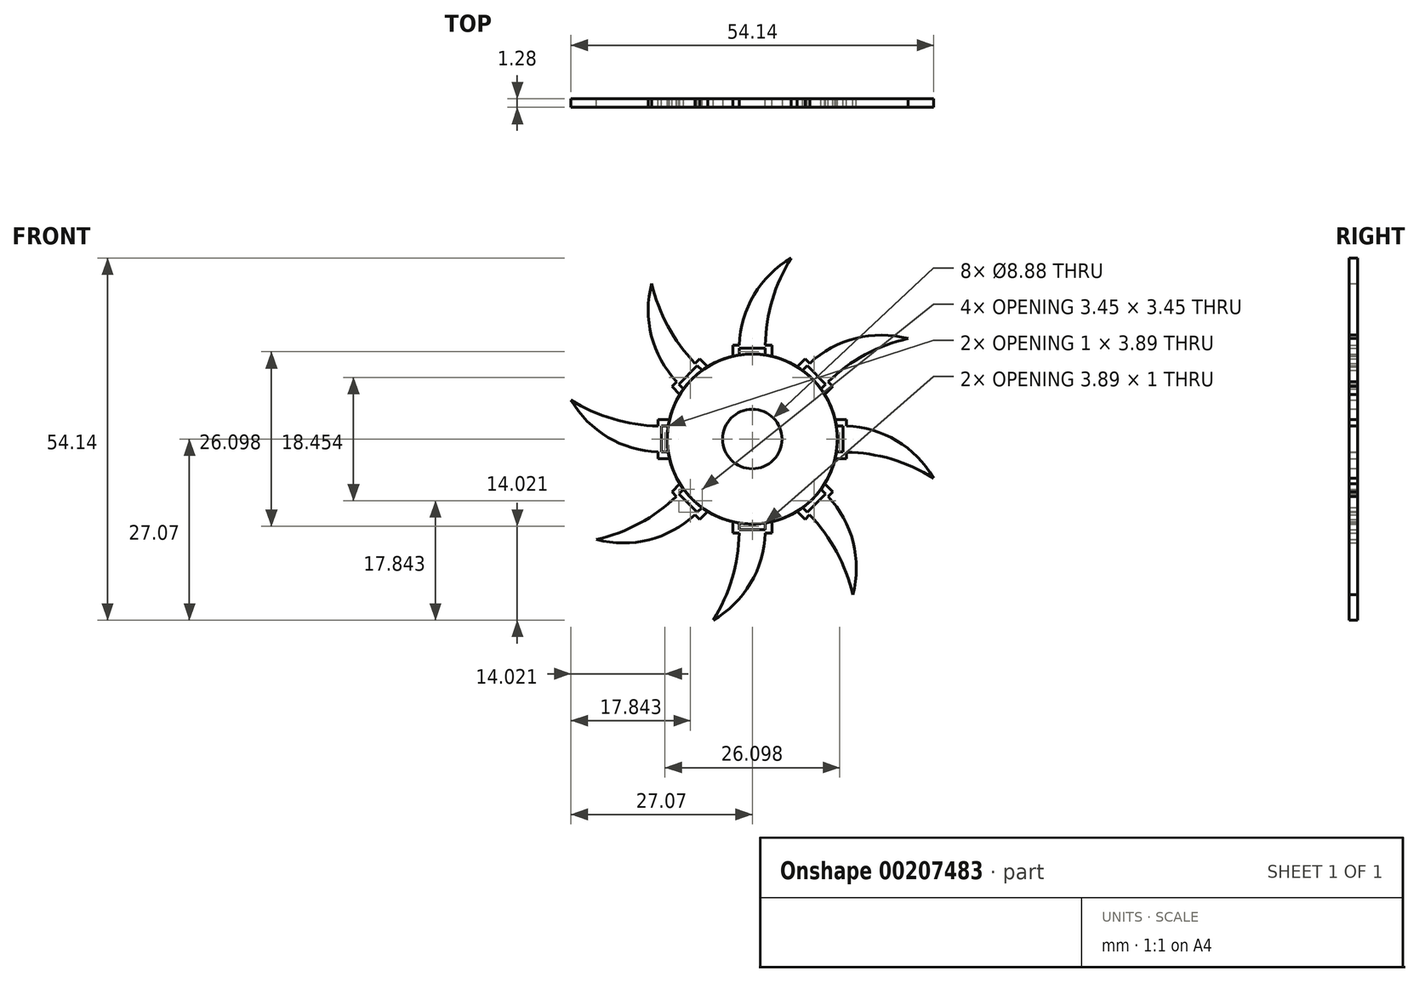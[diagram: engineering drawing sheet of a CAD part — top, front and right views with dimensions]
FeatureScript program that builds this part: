
annotation { "Feature Type Name" : "Feature", "Feature Type Description" : "" }
export const myFeature = defineFeature(function(context is Context, id is Id, definition is map)
    precondition{}
    {
        {
            var Q0;
            Q0=qCreatedBy(makeId("Front.planeOp"),FACE);
            var sketch = newSketch(context, id + "F0", { "sketchPlane" : qUnion([Q0])});
            skCircle(sketch, "E0", {"center": v(0, 0) * mm, "radius": 12.7 * mm});
            skSolve(sketch);
        }
        {
            var Q0;
            Q0=qSketchRegion(id+"F0",true);
            extrude(context, id + "F1", {"entities" : qUnion([Q0]), "endBound" : BoundingType.SYMMETRIC, "depth" : 1.27 * mm});
        }
        {
            var Q0;
            Q0=qCreatedBy(makeId("Front.planeOp"),FACE);
            var sketch = newSketch(context, id + "F2", { "sketchPlane" : qUnion([Q0])});
            skPoint(sketch, "E1.middle", {"position": v(0, 12.38) * mm});
            skLineSegment(sketch, "E2.bottom", {"start": v(1.94, 13.55) * mm, "end": v(-1.94, 13.55) * mm});
            skLineSegment(sketch, "E2.top", {"start": v(1.94, 11.21) * mm, "end": v(-1.94, 11.21) * mm});
            skLineSegment(sketch, "E2.left", {"start": v(1.94, 13.55) * mm, "end": v(1.94, 11.21) * mm});
            skLineSegment(sketch, "E2.right", {"start": v(-1.94, 13.55) * mm, "end": v(-1.94, 11.21) * mm});
            skArc(sketch, "E3", {"start": v(5.83, 27.07) * mm, "mid": v(0.14, 21.34) * mm, "end": v(-1.94, 13.55) * mm});
            skArc(sketch, "E4", {"start": v(5.83, 27.07) * mm, "mid": v(2.93, 20.58) * mm, "end": v(1.94, 13.55) * mm});
            skLineSegment(sketch, "E5.bottom", {"start": v(2.93, 10.7) * mm, "end": v(-2.93, 10.7) * mm});
            skLineSegment(sketch, "E5.top", {"start": v(2.93, 14.05) * mm, "end": v(-2.93, 14.05) * mm});
            skLineSegment(sketch, "E5.left", {"start": v(2.93, 10.7) * mm, "end": v(2.93, 14.05) * mm});
            skLineSegment(sketch, "E5.right", {"start": v(-2.93, 10.7) * mm, "end": v(-2.93, 14.05) * mm});
            skSolve(sketch);
        }
        {
            var Q0;
            Q0=qSketchRegion(id+"F2",true);
            extrude(context, id + "F3", {"entities" : qUnion([Q0]), "operationType" : NewBodyOperationType.ADD, "endBound" : BoundingType.SYMMETRIC, "depth" : 1.27 * mm});
        }
        {
            var Q0;
            Q0=makeQuery(id+"F1.opExtrude","SWEPT_BODY",BODY,{"disambiguationData":[OSD([sQuery(id+"F0.wireOp",EDGE,"E0")])]});
            var Q1;
            Q1=sQuery(id+"F0.wireOp",EDGE,"E0");
            circularPattern(context, id + "F4", {"entities" : qUnion([Q0]), "axis" : qUnion([Q1]), "angle" : 360 * degree, "instanceCount" : 8, "equalSpace" : true});
        }
        {
            var Q0;
            Q0=qCreatedBy(makeId("Front.planeOp"),FACE);
            var sketch = newSketch(context, id + "F5", { "sketchPlane" : qUnion([Q0])});
            skCircle(sketch, "E6", {"center": v(0, 0) * mm, "radius": 4.44 * mm});
            skSolve(sketch);
        }
        {
            var Q0;
            Q0=qSketchRegion(id+"F5",true);
            extrude(context, id + "F6", {"entities" : qUnion([Q0]), "operationType" : NewBodyOperationType.REMOVE, "endBound" : BoundingType.SYMMETRIC, "oppositeDirection" : true, "depth" : 1.27 * mm});
        }
    });
